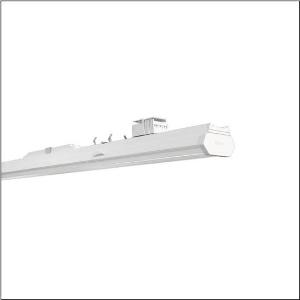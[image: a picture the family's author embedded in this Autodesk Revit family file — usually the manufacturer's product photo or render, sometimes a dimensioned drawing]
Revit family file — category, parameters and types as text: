
# Revit family: licross_r__21_protected_mo_52td12mn4a5g_9007
name_source: partatom
category: Lighting Fixtures
units: mm (PartAtom-declared; Revit-internal decimal feet)

## family parameters
Cut with Voids When Loaded = No
Host = Face
Light Source = No
Part Type = Normal
Room Calculation Point = No
Round Connector Dimension = Use Diameter
Shared = No

## types (1)
- --- (1 x LED, 10750 lm, 60.5 W, 4000K)
    Apparent Load = 61 VA
    CIE Flux Codes = 73 92 98 99 100
    Color Rendering = 80
    Color Temperature = 4000K
    Default Elevation = 1800 mm
    Description = Licross® 21 Protected MO, luminaire insert, of sheet steel, galvanised, coil coated, white, length: 1.500mm, width: 90mm, height: 101mm, LED rated luminous flux: 10.750lm, light colour: 840, control gear: ON/OFF Multilumen, with plug, 3-pole, with phase selection, mains connection: 220..240V, AC, 50/60Hz, rated input power: 61W, halogen-free wiring, primary light control with lens, of plastic, primary optical cover: cover, of PMMA, light emission: direct distribution, primary light characteristic: symmetric, protection rating (complete): IP54, insulation class (complete): insulation class I (protective earthing), certification: CE, ENEC, VDE, UKCA, protection symbol: D if used in an environment with non-conductive dust loads with corresponding accessories, impact resistance: IK06, permissible ambient temperature for indoor applications: -35..+45°C, corresponds to IFS (International Featured Standards) requirements for safety and quality in the food industry, reducing of maximum allowable ambient temperature of 5°C with ceiling mounting, LABS conformity tested according to VDMA 24364:2018-05, packaging unit: 1 piece
    Height = 92 mm
    Lamp = 1 x LED
    Lamp Light Flux = 10750 lm
    Lamp Power = 60.5 W
    Lamp count = 1
    Length = 1500 mm
    Luminous efficacy = 178 lm/W
    Manufacturer = Siteco
    ModVariant = No
    Model = 52TD12MN4A5G
    Mounting Place = Ceiling
    Mounting Type = Pendant
    Number of Poles = 1
    OnlyDefault = Yes
    Power Factor = 1
    Product Name = Licross® 21 Protected MO
    Product group = luminaire insert
    ProductGroupID = 901
    Protection Class = Protection class I
    Protection Degree = IP 54
    RLX_Detail_Level = 1
    RLX_Emergency_Light_Flux = 0 lm
    RLX_Emergency_Type = 0
    RLX_Emergency_Type_DB = No
    RlxData = <blob elided: 22073 chars, md5=ba85c0a5>
    Socket = socket
    Standby Power = 0 W
    System Light Flux = 10750 lm
    System Power = 61 W
    Type Comments = factory setting: luminous flux: 100 % | (A | C | E) | 140 mA
    Type Image = l_1256148.jpg
    URL = http://relux.com
    VarID = @adj_057427
    Voltage = 0 V
    Weight = 0.00 kg
    Width = 88 mm

## geometry (parser evidence)
native form markers: Blend x4, Sweep x10
no freeform markers — native parametric forms only
